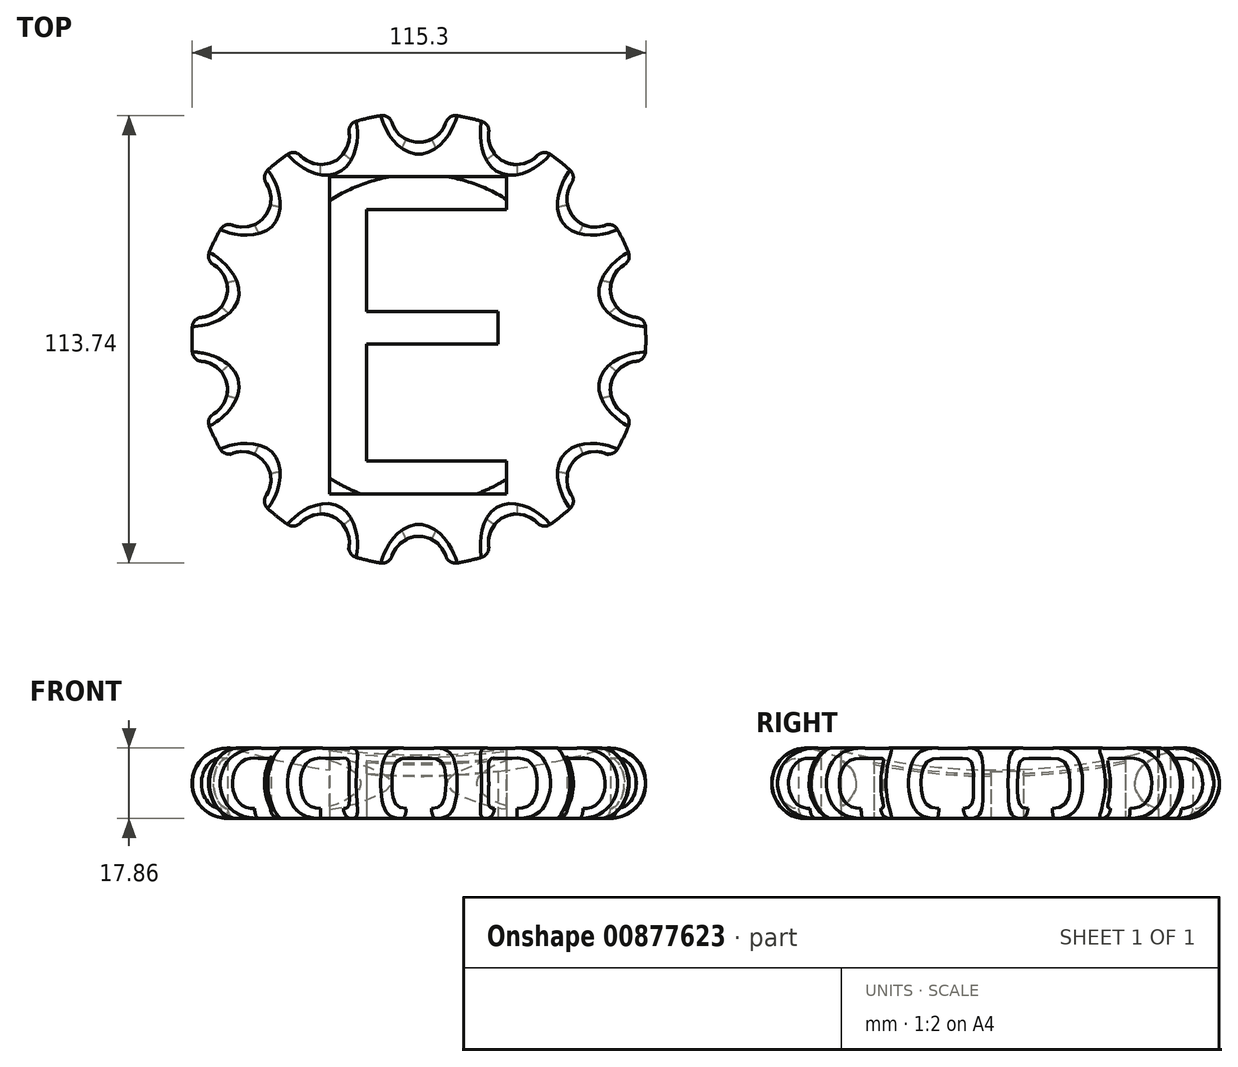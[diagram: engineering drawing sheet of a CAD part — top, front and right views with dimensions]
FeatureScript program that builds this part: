
annotation { "Feature Type Name" : "Feature", "Feature Type Description" : "" }
export const myFeature = defineFeature(function(context is Context, id is Id, definition is map)
    precondition{}
    {
        {
            var Q0;
            Q0=qCreatedBy(makeId("Front.planeOp"),FACE);
            var sketch = newSketch(context, id + "F0", { "sketchPlane" : qUnion([Q0])});
            skArc(sketch, "E0", {"start": v(-46.16, 17.48) * mm, "mid": v(-57.56, 10.22) * mm, "end": v(-48.72, 0) * mm});
            skArc(sketch, "E1", {"start": v(-46.16, 17.48) * mm, "mid": v(-23.33, 12.41) * mm, "end": v(0, 10.71) * mm});
            skLineSegment(sketch, "E2", {"start": v(0, 0) * mm, "end": v(0, 10.71) * mm});
            skLineSegment(sketch, "E3", {"start": v(0, 10.71) * mm, "end": v(0, 0) * mm});
            skLineSegment(sketch, "E4", {"start": v(0, 0) * mm, "end": v(-48.72, 0) * mm});
            skSolve(sketch);
        }
        {
            var Q0;
            Q0=makeQuery(id+"F0.imprint","IMPRINT",FACE,{"disambiguationData":[TD([[makeQuery(id+"F0.imprint","IMPRINT",EDGE,{"derivedFrom":sQuery(id+"F0.wireOp",EDGE,"E0")}),1.0]])]});
            var Q1;
            Q1=sQuery(id+"F0.wireOp",EDGE,"E2");
            revolve(context, id + "F1", {"surfaceOperationType" : NewSurfaceOperationType.NEW, "entities" : qUnion([Q0]), "axis" : qUnion([Q1]), "revolveType" : RevolveType.FULL});
        }
        {
            var Q0;
            Q0=qCreatedBy(makeId("Top.planeOp"),FACE);
            var sketch = newSketch(context, id + "F2", { "sketchPlane" : qUnion([Q0])});
            skText(sketch, "E5", { "text": "E", "fontName": "OpenSans-Regular.ttf"});
            const initialGuessF2  = {"E5": [-0.03371, -0.03926, 1, 0, 0.08128]};
            skSetInitialGuess(sketch, initialGuessF2);
            skSolve(sketch);
        }
        {
            var Q0;
            Q0=qSketchRegion(id+"F2",true);
            var Q1;
            Q1=qSketchRegion(id+"F4",true);
            extrude(context, id + "F3", {"entities" : qUnion([Q0, Q1]), "operationType" : NewBodyOperationType.REMOVE, "depth" : 25.4 * mm, "offsetDistance" : 25.4 * mm});
        }
        {
            var Q0;
            Q0=qCreatedBy(makeId("Top.planeOp"),FACE);
            var sketch = newSketch(context, id + "F4", { "sketchPlane" : qUnion([Q0])});
            skCircle(sketch, "E6", {"center": v(0, 57.23) * mm, "radius": 7.17 * mm});
            skCircle(sketch, "E7.1.0", {"center": v(-24.83, 51.56) * mm, "radius": 7.17 * mm});
            skCircle(sketch, "E7.2.0", {"center": v(-44.74, 35.68) * mm, "radius": 7.17 * mm});
            skCircle(sketch, "E7.3.0", {"center": v(-55.8, 12.73) * mm, "radius": 7.17 * mm});
            skCircle(sketch, "E7.4.0", {"center": v(-55.8, -12.73) * mm, "radius": 7.17 * mm});
            skCircle(sketch, "E7.5.0", {"center": v(-44.74, -35.68) * mm, "radius": 7.17 * mm});
            skCircle(sketch, "E7.6.0", {"center": v(-24.83, -51.56) * mm, "radius": 7.17 * mm});
            skCircle(sketch, "E7.7.0", {"center": v(0, -57.23) * mm, "radius": 7.17 * mm});
            skCircle(sketch, "E7.8.0", {"center": v(24.83, -51.56) * mm, "radius": 7.17 * mm});
            skCircle(sketch, "E7.9.0", {"center": v(44.74, -35.68) * mm, "radius": 7.17 * mm});
            skPoint(sketch, "E7.center", {"position": v(0, 0) * mm});
            skCircle(sketch, "E8.1.10.0", {"center": v(55.8, -12.73) * mm, "radius": 7.17 * mm});
            skCircle(sketch, "E9.1.11.0", {"center": v(55.8, 12.73) * mm, "radius": 7.17 * mm});
            skCircle(sketch, "E9.1.12.0", {"center": v(44.74, 35.68) * mm, "radius": 7.17 * mm});
            skCircle(sketch, "E9.1.13.0", {"center": v(24.83, 51.56) * mm, "radius": 7.17 * mm});
            skSolve(sketch);
        }
        {
            var Q0;
            Q0=qCreatedBy(makeId("Front.planeOp"),FACE);
            var sketch = newSketch(context, id + "F5", { "sketchPlane" : qUnion([Q0])});
            skCircle(sketch, "E10", {"center": v(-48.72, 8.93) * mm, "radius": 6.79 * mm});
            skSolve(sketch);
        }
        {
            var Q0;
            Q0=qSketchRegion(id+"F5",true);
            var Q1;
            Q1=sQuery(id+"F0.wireOp",EDGE,"E2");
            revolve(context, id + "F6", {"operationType" : NewBodyOperationType.ADD, "surfaceOperationType" : NewSurfaceOperationType.NEW, "entities" : qUnion([Q0]), "axis" : qUnion([Q1]), "revolveType" : RevolveType.FULL});
        }
        {
            var Q0;
            Q0=qSketchRegion(id+"F4",true);
            extrude(context, id + "F7", {"entities" : qUnion([Q0]), "operationType" : NewBodyOperationType.REMOVE, "depth" : 25.4 * mm, "offsetDistance" : 25.4 * mm});
        }
        {
            var Q0;
            Q0=makeQuery(id+"F7.boolean.opBoolean","INTERSECT",EDGE,{"derivedFrom":[makeQuery(id+"F1.opRevolve","SWEPT_FACE",FACE,{"disambiguationData":[OSD([sQuery(id+"F0.wireOp",EDGE,"E0")])]}),makeQuery(id+"F7.opExtrude","SWEPT_FACE",FACE,{"disambiguationData":[OSD([sQuery(id+"F4.wireOp",EDGE,"E9.1.12.0")])]})]});
            var Q1;
            Q1=makeQuery(id+"F7.boolean.opBoolean","INTERSECT",EDGE,{"derivedFrom":[makeQuery(id+"F1.opRevolve","SWEPT_FACE",FACE,{"disambiguationData":[OSD([sQuery(id+"F0.wireOp",EDGE,"E0")])]}),makeQuery(id+"F7.opExtrude","SWEPT_FACE",FACE,{"disambiguationData":[OSD([sQuery(id+"F4.wireOp",EDGE,"E9.1.13.0")])]})]});
            var Q2;
            Q2=makeQuery(id+"F7.boolean.opBoolean","INTERSECT",EDGE,{"derivedFrom":[makeQuery(id+"F1.opRevolve","SWEPT_FACE",FACE,{"disambiguationData":[OSD([sQuery(id+"F0.wireOp",EDGE,"E0")])]}),makeQuery(id+"F7.opExtrude","SWEPT_FACE",FACE,{"disambiguationData":[OSD([sQuery(id+"F4.wireOp",EDGE,"E6")])]})]});
            var Q3;
            Q3=makeQuery(id+"F7.boolean.opBoolean","INTERSECT",EDGE,{"derivedFrom":[makeQuery(id+"F1.opRevolve","SWEPT_FACE",FACE,{"disambiguationData":[OSD([sQuery(id+"F0.wireOp",EDGE,"E0")])]}),makeQuery(id+"F7.opExtrude","SWEPT_FACE",FACE,{"disambiguationData":[OSD([sQuery(id+"F4.wireOp",EDGE,"E7.4.0")])]})]});
            var Q4;
            Q4=makeQuery(id+"F7.boolean.opBoolean","INTERSECT",EDGE,{"derivedFrom":[makeQuery(id+"F1.opRevolve","SWEPT_FACE",FACE,{"disambiguationData":[OSD([sQuery(id+"F0.wireOp",EDGE,"E0")])]}),makeQuery(id+"F7.opExtrude","SWEPT_FACE",FACE,{"disambiguationData":[OSD([sQuery(id+"F4.wireOp",EDGE,"E7.5.0")])]})]});
            var Q5;
            Q5=makeQuery(id+"F7.boolean.opBoolean","INTERSECT",EDGE,{"derivedFrom":[makeQuery(id+"F1.opRevolve","SWEPT_FACE",FACE,{"disambiguationData":[OSD([sQuery(id+"F0.wireOp",EDGE,"E0")])]}),makeQuery(id+"F7.opExtrude","SWEPT_FACE",FACE,{"disambiguationData":[OSD([sQuery(id+"F4.wireOp",EDGE,"E7.5.0")])]})]});
            var Q6;
            Q6=makeQuery(id+"F7.boolean.opBoolean","INTERSECT",EDGE,{"derivedFrom":[makeQuery(id+"F1.opRevolve","SWEPT_FACE",FACE,{"disambiguationData":[OSD([sQuery(id+"F0.wireOp",EDGE,"E0")])]}),makeQuery(id+"F7.opExtrude","SWEPT_FACE",FACE,{"disambiguationData":[OSD([sQuery(id+"F4.wireOp",EDGE,"E7.6.0")])]})]});
            var Q7;
            Q7=makeQuery(id+"F7.boolean.opBoolean","INTERSECT",EDGE,{"derivedFrom":[makeQuery(id+"F1.opRevolve","SWEPT_FACE",FACE,{"disambiguationData":[OSD([sQuery(id+"F0.wireOp",EDGE,"E0")])]}),makeQuery(id+"F7.opExtrude","SWEPT_FACE",FACE,{"disambiguationData":[OSD([sQuery(id+"F4.wireOp",EDGE,"E7.7.0")])]})]});
            var Q8;
            Q8=makeQuery(id+"F7.boolean.opBoolean","INTERSECT",EDGE,{"derivedFrom":[makeQuery(id+"F1.opRevolve","SWEPT_FACE",FACE,{"disambiguationData":[OSD([sQuery(id+"F0.wireOp",EDGE,"E0")])]}),makeQuery(id+"F7.opExtrude","SWEPT_FACE",FACE,{"disambiguationData":[OSD([sQuery(id+"F4.wireOp",EDGE,"E7.8.0")])]})]});
            var Q9;
            Q9=makeQuery(id+"F7.boolean.opBoolean","INTERSECT",EDGE,{"derivedFrom":[makeQuery(id+"F1.opRevolve","SWEPT_FACE",FACE,{"disambiguationData":[OSD([sQuery(id+"F0.wireOp",EDGE,"E0")])]}),makeQuery(id+"F7.opExtrude","SWEPT_FACE",FACE,{"disambiguationData":[OSD([sQuery(id+"F4.wireOp",EDGE,"E7.6.0")])]})]});
            var Q10;
            Q10=makeQuery(id+"F7.boolean.opBoolean","INTERSECT",EDGE,{"derivedFrom":[makeQuery(id+"F1.opRevolve","SWEPT_FACE",FACE,{"disambiguationData":[OSD([sQuery(id+"F0.wireOp",EDGE,"E0")])]}),makeQuery(id+"F7.opExtrude","SWEPT_FACE",FACE,{"disambiguationData":[OSD([sQuery(id+"F4.wireOp",EDGE,"E7.7.0")])]})]});
            var Q11;
            Q11=makeQuery(id+"F7.boolean.opBoolean","INTERSECT",EDGE,{"derivedFrom":[makeQuery(id+"F1.opRevolve","SWEPT_FACE",FACE,{"disambiguationData":[OSD([sQuery(id+"F0.wireOp",EDGE,"E0")])]}),makeQuery(id+"F7.opExtrude","SWEPT_FACE",FACE,{"disambiguationData":[OSD([sQuery(id+"F4.wireOp",EDGE,"E7.8.0")])]})]});
            var Q12;
            Q12=makeQuery(id+"F7.boolean.opBoolean","INTERSECT",EDGE,{"derivedFrom":[makeQuery(id+"F1.opRevolve","SWEPT_FACE",FACE,{"disambiguationData":[OSD([sQuery(id+"F0.wireOp",EDGE,"E0")])]}),makeQuery(id+"F7.opExtrude","SWEPT_FACE",FACE,{"disambiguationData":[OSD([sQuery(id+"F4.wireOp",EDGE,"E7.9.0")])]})]});
            var Q13;
            Q13=makeQuery(id+"F7.boolean.opBoolean","INTERSECT",EDGE,{"derivedFrom":[makeQuery(id+"F1.opRevolve","SWEPT_FACE",FACE,{"disambiguationData":[OSD([sQuery(id+"F0.wireOp",EDGE,"E0")])]}),makeQuery(id+"F7.opExtrude","SWEPT_FACE",FACE,{"disambiguationData":[OSD([sQuery(id+"F4.wireOp",EDGE,"E8.1.10.0")])]})]});
            var Q14;
            Q14=makeQuery(id+"F7.boolean.opBoolean","INTERSECT",EDGE,{"derivedFrom":[makeQuery(id+"F1.opRevolve","SWEPT_FACE",FACE,{"disambiguationData":[OSD([sQuery(id+"F0.wireOp",EDGE,"E0")])]}),makeQuery(id+"F7.opExtrude","SWEPT_FACE",FACE,{"disambiguationData":[OSD([sQuery(id+"F4.wireOp",EDGE,"E9.1.11.0")])]})]});
            var Q15;
            Q15=makeQuery(id+"F7.boolean.opBoolean","INTERSECT",EDGE,{"derivedFrom":[makeQuery(id+"F1.opRevolve","SWEPT_FACE",FACE,{"disambiguationData":[OSD([sQuery(id+"F0.wireOp",EDGE,"E0")])]}),makeQuery(id+"F7.opExtrude","SWEPT_FACE",FACE,{"disambiguationData":[OSD([sQuery(id+"F4.wireOp",EDGE,"E7.7.0")])]})]});
            var Q16;
            Q16=makeQuery(id+"F7.boolean.opBoolean","INTERSECT",EDGE,{"derivedFrom":[makeQuery(id+"F1.opRevolve","SWEPT_FACE",FACE,{"disambiguationData":[OSD([sQuery(id+"F0.wireOp",EDGE,"E0")])]}),makeQuery(id+"F7.opExtrude","SWEPT_FACE",FACE,{"disambiguationData":[OSD([sQuery(id+"F4.wireOp",EDGE,"E7.8.0")])]})]});
            var Q17;
            Q17=makeQuery(id+"F7.boolean.opBoolean","INTERSECT",EDGE,{"derivedFrom":[makeQuery(id+"F1.opRevolve","SWEPT_FACE",FACE,{"disambiguationData":[OSD([sQuery(id+"F0.wireOp",EDGE,"E0")])]}),makeQuery(id+"F7.opExtrude","SWEPT_FACE",FACE,{"disambiguationData":[OSD([sQuery(id+"F4.wireOp",EDGE,"E7.9.0")])]})]});
            var Q18;
            Q18=makeQuery(id+"F7.boolean.opBoolean","INTERSECT",EDGE,{"derivedFrom":[makeQuery(id+"F1.opRevolve","SWEPT_FACE",FACE,{"disambiguationData":[OSD([sQuery(id+"F0.wireOp",EDGE,"E0")])]}),makeQuery(id+"F7.opExtrude","SWEPT_FACE",FACE,{"disambiguationData":[OSD([sQuery(id+"F4.wireOp",EDGE,"E7.8.0")])]})]});
            var Q19;
            Q19=makeQuery(id+"F7.boolean.opBoolean","INTERSECT",EDGE,{"derivedFrom":[makeQuery(id+"F1.opRevolve","SWEPT_FACE",FACE,{"disambiguationData":[OSD([sQuery(id+"F0.wireOp",EDGE,"E0")])]}),makeQuery(id+"F7.opExtrude","SWEPT_FACE",FACE,{"disambiguationData":[OSD([sQuery(id+"F4.wireOp",EDGE,"E7.8.0")])]})]});
            var Q20;
            Q20=makeQuery(id+"F7.boolean.opBoolean","INTERSECT",EDGE,{"derivedFrom":[makeQuery(id+"F1.opRevolve","SWEPT_FACE",FACE,{"disambiguationData":[OSD([sQuery(id+"F0.wireOp",EDGE,"E0")])]}),makeQuery(id+"F7.opExtrude","SWEPT_FACE",FACE,{"disambiguationData":[OSD([sQuery(id+"F4.wireOp",EDGE,"E7.8.0")])]})]});
            fillet(context, id + "F8", {"entities" : qUnion([Q0, Q1, Q2, Q3, Q4, Q5, Q6, Q7, Q8, Q9, Q10, Q11, Q12, Q13, Q14, Q15, Q16, Q17, Q18, Q19, Q20]), "radius" : 2.54 * mm, "tangentPropagation" : true, "allowEdgeOverflow" : false});
        }
        {
            var Q0;
            Q0=makeQuery(id+"F7.boolean.opBoolean","INTERSECT",EDGE,{"derivedFrom":[makeQuery(id+"F1.opRevolve","SWEPT_FACE",FACE,{"disambiguationData":[OSD([sQuery(id+"F0.wireOp",EDGE,"E0")])]}),makeQuery(id+"F7.opExtrude","SWEPT_FACE",FACE,{"disambiguationData":[OSD([sQuery(id+"F4.wireOp",EDGE,"E7.1.0")])]})]});
            var Q1;
            Q1=makeQuery(id+"F7.boolean.opBoolean","INTERSECT",EDGE,{"derivedFrom":[makeQuery(id+"F1.opRevolve","SWEPT_FACE",FACE,{"disambiguationData":[OSD([sQuery(id+"F0.wireOp",EDGE,"E0")])]}),makeQuery(id+"F7.opExtrude","SWEPT_FACE",FACE,{"disambiguationData":[OSD([sQuery(id+"F4.wireOp",EDGE,"E7.2.0")])]})]});
            var Q2;
            Q2=makeQuery(id+"F7.boolean.opBoolean","INTERSECT",EDGE,{"derivedFrom":[makeQuery(id+"F1.opRevolve","SWEPT_FACE",FACE,{"disambiguationData":[OSD([sQuery(id+"F0.wireOp",EDGE,"E0")])]}),makeQuery(id+"F7.opExtrude","SWEPT_FACE",FACE,{"disambiguationData":[OSD([sQuery(id+"F4.wireOp",EDGE,"E7.3.0")])]})]});
            fillet(context, id + "F9", {"entities" : qUnion([Q0, Q1, Q2]), "radius" : 2.54 * mm, "tangentPropagation" : true, "allowEdgeOverflow" : false});
        }
    });
